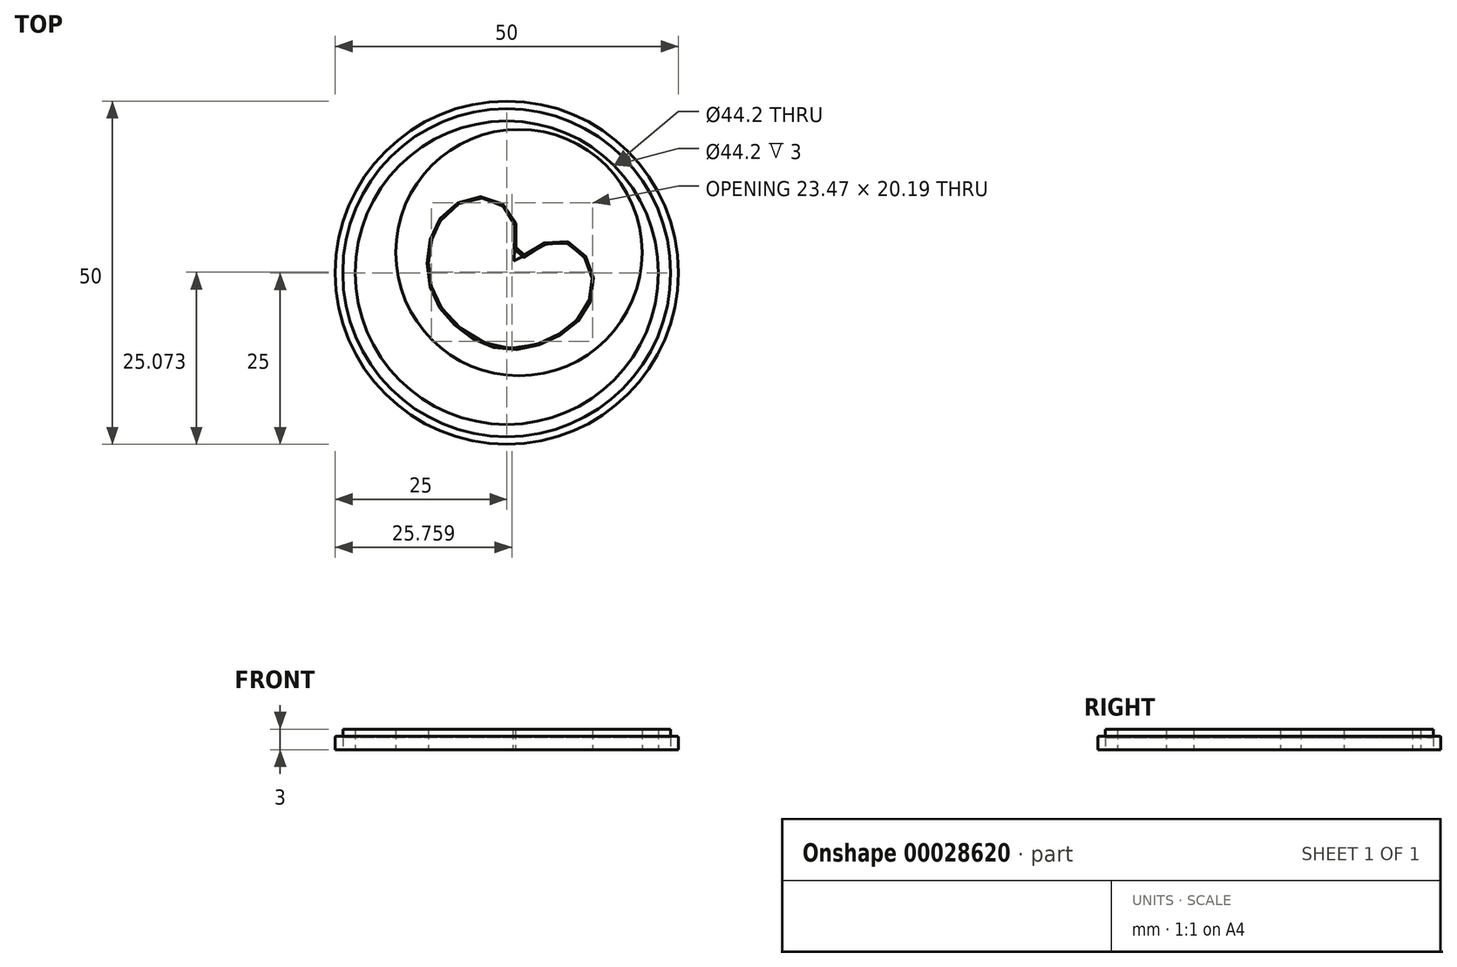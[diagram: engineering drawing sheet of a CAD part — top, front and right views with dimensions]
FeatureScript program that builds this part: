
annotation { "Feature Type Name" : "Feature", "Feature Type Description" : "" }
export const myFeature = defineFeature(function(context is Context, id is Id, definition is map)
    precondition{}
    {
        {
            var Q0;
            Q0=qCreatedBy(makeId("Top.planeOp"),FACE);
            var sketch = newSketch(context, id + "F0", { "sketchPlane" : qUnion([Q0])});
            skCircle(sketch, "E0", {"center": v(0, 0) * mm, "radius": 25 * mm});
            skCircle(sketch, "E1", {"center": v(0, 0) * mm, "radius": 23.9 * mm});
            skCircle(sketch, "E2", {"center": v(0, 0) * mm, "radius": 22.1 * mm});
            skCircle(sketch, "E3", {"center": v(1.78, 2.94) * mm, "radius": 17.95 * mm});
            skPoint(sketch, "E4", {"position": v(0, 25) * mm});
            skPoint(sketch, "E5", {"position": v(0, 20.8) * mm});
            skPoint(sketch, "E6", {"position": v(-15.93, 0) * mm});
            skPoint(sketch, "E7", {"position": v(-25, 0) * mm});
            skLineSegment(sketch, "E8", {"start": v(0.34, 31.79) * mm, "end": v(0.34, -39.78) * mm, "construction": true});
            skPoint(sketch, "E9", {"position": v(0.34, 0) * mm});
            skPoint(sketch, "E10", {"position": v(-3.9, 10.89) * mm});
            skPoint(sketch, "E11", {"position": v(12.51, -1.48) * mm});
            skPoint(sketch, "E12", {"position": v(0.65, -11.01) * mm});
            skPoint(sketch, "E13", {"position": v(-11.43, 1.18) * mm});
            skFitSpline(sketch, "E14", {"points": [v(-10.98, -2) * mm, v(-11.37, -0.01) * mm, v(-11.4, 1.98) * mm, v(-11.15, 3.98) * mm, v(-10.56, 5.9) * mm, v(-10.17, 6.73) * mm, v(-9.73, 7.55) * mm, v(-8.59, 8.96) * mm, v(-6.33, 10.35) * mm, v(-4.5, 10.86) * mm, v(-2.83, 10.77) * mm, v(-1.23, 10.17) * mm, v(0.23, 9.1) * mm, v(0.95, 7.82) * mm, v(1.27, 6.13) * mm, v(1.18, 4) * mm, v(0.99, 2.8) * mm, v(0.86, 2.24) * mm, v(0.93, 1.94) * mm, v(1.1, 1.73) * mm, v(1.55, 1.62) * mm, v(1.95, 1.8) * mm, v(3.45, 2.98) * mm, v(4.68, 3.75) * mm, v(6.04, 4.35) * mm, v(7.5, 4.61) * mm, v(8.89, 4.32) * mm, v(10.24, 3.45) * mm, v(11.54, 2.03) * mm, v(12.21, 0.64) * mm, v(12.5, -1.02) * mm, v(12.48, -2.05) * mm, v(12.07, -3.85) * mm, v(11.28, -5.48) * mm, v(10.26, -6.9) * mm, v(8.96, -8.07) * mm, v(7.48, -9.04) * mm, v(5.93, -9.85) * mm, v(2.94, -10.82) * mm, v(0.92, -11) * mm, v(-1.1, -10.87) * mm, v(-3.45, -10.13) * mm, v(-5.61, -8.95) * mm, v(-8.2, -6.79) * mm, v(-9.57, -5.06) * mm, v(-10.6, -3.07) * mm, v(-10.98, -2) * mm]});
            skLineSegment(sketch, "E15", {"start": v(-11.43, 18.63) * mm, "end": v(-11.43, -20.08) * mm, "construction": true});
            skLineSegment(sketch, "E16", {"start": v(-26.76, 10.89) * mm, "end": v(26.59, 10.89) * mm, "construction": true});
            skLineSegment(sketch, "E17", {"start": v(12.51, 19.74) * mm, "end": v(12.51, -18.58) * mm, "construction": true});
            skLineSegment(sketch, "E18", {"start": v(26.08, -11.01) * mm, "end": v(-24.25, -11.01) * mm, "construction": true});
            skSolve(sketch);
        }
        {
            var Q0;
            Q0=makeQuery(id+"F0.imprint","IMPRINT",FACE,{"disambiguationData":[TD([[makeQuery(id+"F0.imprint","IMPRINT",EDGE,{"derivedFrom":sQuery(id+"F0.wireOp",EDGE,"E14")}),-1.0]])]});
            extrude(context, id + "F1", {"entities" : qUnion([Q0]), "depth" : 2 * mm});
        }
        {
            var Q0;
            Q0=makeQuery(id+"F1.opExtrude","CAP_EDGE",EDGE,{"disambiguationData":[OSD([sQuery(id+"F0.wireOp",EDGE,"E14")])],"isStart":true});
            fillet(context, id + "F2", {"entities" : qUnion([Q0]), "radius" : .2 * mm, "tangentPropagation" : true, "allowEdgeOverflow" : false});
        }
        {
            var Q0;
            Q0=makeQuery(id+"F0.imprint","IMPRINT",FACE,{"disambiguationData":[TD([[makeQuery(id+"F0.imprint","IMPRINT",EDGE,{"derivedFrom":sQuery(id+"F0.wireOp",EDGE,"E0")}),1.0]])]});
            var Q1;
            Q1=makeQuery(id+"F0.imprint","IMPRINT",FACE,{"disambiguationData":[TD([[makeQuery(id+"F0.imprint","IMPRINT",EDGE,{"derivedFrom":sQuery(id+"F0.wireOp",EDGE,"E2")}),1.0]])]});
            extrude(context, id + "F3", {"entities" : qUnion([Q0, Q1]), "depth" : 2 * mm});
        }
        {
            var Q0;
            Q0=makeQuery(id+"F3.opExtrude","CAP_EDGE",EDGE,{"disambiguationData":[OSD([sQuery(id+"F0.wireOp",EDGE,"E2")])],"isStart":false});
            var Q1;
            Q1=makeQuery(id+"F3.opExtrude","CAP_EDGE",EDGE,{"disambiguationData":[OSD([sQuery(id+"F0.wireOp",EDGE,"E3")])],"isStart":false});
            var Q2;
            Q2=makeQuery(id+"F3.opExtrude","CAP_EDGE",EDGE,{"disambiguationData":[OSD([sQuery(id+"F0.wireOp",EDGE,"E1")])],"isStart":false});
            var Q3;
            Q3=makeQuery(id+"F3.opExtrude","CAP_EDGE",EDGE,{"disambiguationData":[OSD([sQuery(id+"F0.wireOp",EDGE,"E0")])],"isStart":false});
            fillet(context, id + "F4", {"entities" : qUnion([Q0, Q1, Q2, Q3]), "radius" : .2 * mm, "tangentPropagation" : true, "allowEdgeOverflow" : false});
        }
        {
            var Q0;
            Q0=makeQuery(id+"F0.imprint","IMPRINT",FACE,{"disambiguationData":[TD([[makeQuery(id+"F0.imprint","IMPRINT",EDGE,{"derivedFrom":sQuery(id+"F0.wireOp",EDGE,"E0")}),1.0]])]});
            extrude(context, id + "F5", {"entities" : qUnion([Q0]), "depth" : 1 * mm});
        }
        {
            var Q0;
            Q0=makeQuery(id+"F0.imprint","IMPRINT",FACE,{"disambiguationData":[TD([[makeQuery(id+"F0.imprint","IMPRINT",EDGE,{"derivedFrom":sQuery(id+"F0.wireOp",EDGE,"E1")}),1.0]])]});
            extrude(context, id + "F6", {"entities" : qUnion([Q0]), "operationType" : NewBodyOperationType.ADD, "depth" : 3 * mm});
        }
        {
            var Q0;
            Q0=makeQuery(id+"F0.imprint","IMPRINT",FACE,{"disambiguationData":[TD([[makeQuery(id+"F0.imprint","IMPRINT",EDGE,{"derivedFrom":sQuery(id+"F0.wireOp",EDGE,"E2")}),1.0]])]});
            extrude(context, id + "F7", {"entities" : qUnion([Q0]), "operationType" : NewBodyOperationType.ADD, "depth" : 1 * mm});
        }
        {
            var Q0;
            Q0=makeQuery(id+"F0.imprint","IMPRINT",FACE,{"disambiguationData":[TD([[makeQuery(id+"F0.imprint","IMPRINT",EDGE,{"derivedFrom":sQuery(id+"F0.wireOp",EDGE,"E3")}),1.0]])]});
            extrude(context, id + "F8", {"entities" : qUnion([Q0]), "operationType" : NewBodyOperationType.ADD, "depth" : 3 * mm});
        }
        {
            var Q0;
            Q0=makeQuery(id+"F0.imprint","IMPRINT",FACE,{"disambiguationData":[TD([[makeQuery(id+"F0.imprint","IMPRINT",EDGE,{"derivedFrom":sQuery(id+"F0.wireOp",EDGE,"E14")}),-1.0]])]});
            extrude(context, id + "F9", {"entities" : qUnion([Q0]), "operationType" : NewBodyOperationType.ADD, "depth" : 1 * mm});
        }
        {
            var Q0;
            Q0=makeQuery(id+"F6.opExtrude","CAP_EDGE",EDGE,{"disambiguationData":[OSD([sQuery(id+"F0.wireOp",EDGE,"E1")])],"isStart":false});
            var Q1;
            Q1=makeQuery(id+"F6.opExtrude","CAP_EDGE",EDGE,{"disambiguationData":[OSD([sQuery(id+"F0.wireOp",EDGE,"E2")])],"isStart":false});
            var Q2;
            Q2=makeQuery(id+"F8.opExtrude","CAP_EDGE",EDGE,{"disambiguationData":[OSD([sQuery(id+"F0.wireOp",EDGE,"E3")])],"isStart":false});
            var Q3;
            Q3=makeQuery(id+"F8.opExtrude","CAP_EDGE",EDGE,{"disambiguationData":[OSD([sQuery(id+"F0.wireOp",EDGE,"E14")])],"isStart":false});
            fillet(context, id + "F10", {"entities" : qUnion([Q0, Q1, Q2, Q3]), "radius" : .2 * mm, "tangentPropagation" : true, "allowEdgeOverflow" : false});
        }
        {
            var Q0;
            Q0=makeQuery(id+"F0.imprint","IMPRINT",FACE,{"disambiguationData":[TD([[makeQuery(id+"F0.imprint","IMPRINT",EDGE,{"derivedFrom":sQuery(id+"F0.wireOp",EDGE,"E3")}),1.0]])]});
            var Q1;
            Q1=makeQuery(id+"F0.imprint","IMPRINT",FACE,{"disambiguationData":[TD([[makeQuery(id+"F0.imprint","IMPRINT",EDGE,{"derivedFrom":sQuery(id+"F0.wireOp",EDGE,"E1")}),1.0]])]});
            extrude(context, id + "F11", {"entities" : qUnion([Q0, Q1]), "depth" : 3 * mm});
        }
    });
